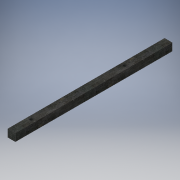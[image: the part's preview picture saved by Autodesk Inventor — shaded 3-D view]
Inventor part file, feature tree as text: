
AUTODESK INVENTOR PART (.ipt)
format: ipt  version: 2019 (Build 230136000, 136)  size: 113,152 bytes
history: native  units: mm
features: extrude x2, sketch x2
ambient origin geometry x8: Origin, YZ Plane, XZ Plane, XY Plane, X Axis, Y Axis, Z Axis, Center Point
bodies: Solid1 (feature_tree)
feature tree (4):
  extrude  "Extrusion1"  Depth=395.0mm
  extrude  "Extrusion2"  Depth=19.0mm
  sketch  "Sketch1"  dims[d0=19.0mm d1=395.0mm]
  sketch  "Sketch2"  dims[d2=19.0mm d3=0.0mm d4=8.0mm d5=8.0mm d6=50.0mm d7=9.5mm d8=9.5mm d10=19.0mm d11=0.0mm d12=235.0mm]
